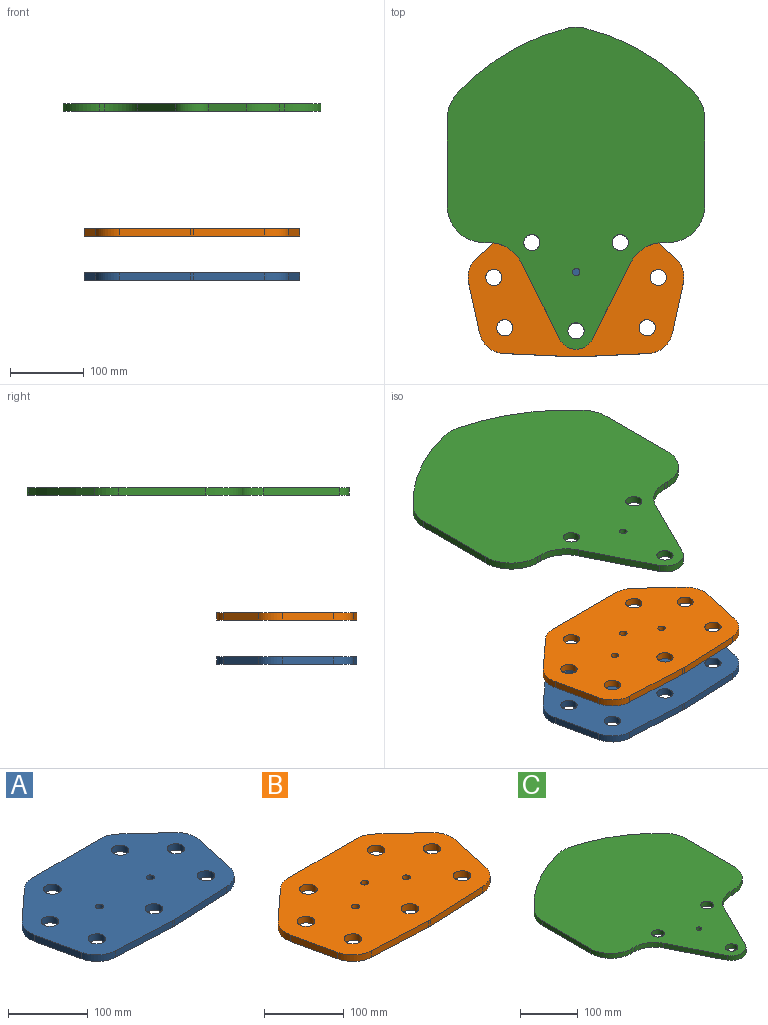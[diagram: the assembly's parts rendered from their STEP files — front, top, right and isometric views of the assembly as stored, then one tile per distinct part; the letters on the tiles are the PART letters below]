
ASSEMBLY  parts=3 mates=2
PART A: 25 faces, bbox 293.4x190x10 mm
  f0: cylinder r=35mm len=10mm, axis (0,0,-1), area 32.2mm2, adj f1,f20,f23,f24
  f1: plane 96.71x10mm, normal (0.05,-1,0), area 968.2mm2, adj f0,f2,f23,f24
  f2: cylinder r=35mm len=32.58mm, axis (0,0,-1), area 458.1mm2, adj f1,f3,f23,f24
  f3: plane 68.37x15mm, normal (0.98,-0.21,0), area 700mm2, adj f2,f4,f23,f24
  f4: cylinder r=35mm len=33.36mm, axis (0,0,-1), area 366.5mm2, adj f3,f5,f23,f24
  f5: plane 51.71x47.18mm, normal (0.67,0.74,0), area 700mm2, adj f4,f6,f23,f24
  f6: cylinder r=35mm len=23.59mm, axis (0,0,-1), area 258.8mm2, adj f5,f7,f23,f24
  f7: plane 120x10mm, normal (0,1,0), area 1200mm2, adj f6,f8,f23,f24
  f8: cylinder r=35mm len=23.59mm, axis (0,0,-1), area 258.8mm2, adj f7,f9,f23,f24
  f9: plane 51.71x47.18mm, normal (-0.67,0.74,0), area 700mm2, adj f8,f10,f23,f24
  f10: cylinder r=35mm len=33.36mm, axis (0,0,-1), area 366.5mm2, adj f9,f11,f23,f24
  f11: plane 68.37x15mm, normal (-0.98,-0.21,0), area 700mm2, adj f10,f12,f23,f24
  f12: cylinder r=35mm len=32.58mm, axis (0,0,-1), area 458.1mm2, adj f11,f20,f23,f24
  f13: cylinder r=5mm len=10mm, axis (0,0,-1), area 314.2mm2, adj f23,f24
  f14: cylinder r=11mm len=22mm, axis (0,0,-1), area 691.2mm2, adj f23,f24
  f15: cylinder r=11mm len=22mm, axis (0,0,-1), area 691.2mm2, adj f23,f24
  f16: cylinder r=11mm len=22mm, axis (0,0,-1), area 691.2mm2, adj f23,f24
  f17: cylinder r=11mm len=22mm, axis (0,0,-1), area 691.2mm2, adj f23,f24
  f18: cylinder r=11mm len=22mm, axis (0,0,-1), area 691.2mm2, adj f23,f24
  f19: cylinder r=11mm len=22mm, axis (0,0,-1), area 691.2mm2, adj f23,f24
  f20: plane 96.71x10mm, normal (-0.05,-1,0), area 968.2mm2, adj f0,f12,f23,f24
  f21: cylinder r=11mm len=22mm, axis (0,0,-1), area 691.2mm2, adj f23,f24
  f22: cylinder r=5mm len=10mm, axis (0,0,-1), area 314.2mm2, adj f23,f24
  f23: plane 293.43x190mm, normal (0,0,1), area 44589.8mm2, adj f0,f1,f2,f3,f4,f5,f6,f7
  f24: plane 293.43x190mm, normal (0,0,-1), area 44589.8mm2, adj f0,f1,f2,f3,f4,f5,f6,f7
PART B: 26 faces, bbox 293.4x190x10 mm
  f0: cylinder r=35mm len=10mm, axis (0,0,-1), area 32.2mm2, adj f1,f21,f24,f25
  f1: plane 96.71x10mm, normal (0.05,-1,0), area 968.2mm2, adj f0,f2,f24,f25
  f2: cylinder r=35mm len=32.58mm, axis (0,0,-1), area 458.1mm2, adj f1,f3,f24,f25
  f3: plane 68.37x15mm, normal (0.98,-0.21,0), area 700mm2, adj f2,f4,f24,f25
  f4: cylinder r=35mm len=33.36mm, axis (0,0,-1), area 366.5mm2, adj f3,f5,f24,f25
  f5: plane 51.71x47.18mm, normal (0.67,0.74,0), area 700mm2, adj f4,f6,f24,f25
  f6: cylinder r=35mm len=23.59mm, axis (0,0,-1), area 258.8mm2, adj f5,f7,f24,f25
  f7: plane 120x10mm, normal (0,1,0), area 1200mm2, adj f6,f8,f24,f25
  f8: cylinder r=35mm len=23.59mm, axis (0,0,-1), area 258.8mm2, adj f7,f9,f24,f25
  f9: plane 51.71x47.18mm, normal (-0.67,0.74,0), area 700mm2, adj f8,f10,f24,f25
  f10: cylinder r=35mm len=33.36mm, axis (0,0,-1), area 366.5mm2, adj f9,f11,f24,f25
  f11: plane 68.37x15mm, normal (-0.98,-0.21,0), area 700mm2, adj f10,f12,f24,f25
  f12: cylinder r=35mm len=32.58mm, axis (0,0,-1), area 458.1mm2, adj f11,f21,f24,f25
  f13: cylinder r=5mm len=10mm, axis (0,0,-1), area 314.2mm2, adj f24,f25
  f14: cylinder r=5mm len=10mm, axis (0,0,-1), area 314.2mm2, adj f24,f25
  f15: cylinder r=11mm len=22mm, axis (0,0,-1), area 691.2mm2, adj f24,f25
  f16: cylinder r=11mm len=22mm, axis (0,0,-1), area 691.2mm2, adj f24,f25
  f17: cylinder r=11mm len=22mm, axis (0,0,-1), area 691.2mm2, adj f24,f25
  f18: cylinder r=11mm len=22mm, axis (0,0,-1), area 691.2mm2, adj f24,f25
  f19: cylinder r=11mm len=22mm, axis (0,0,-1), area 691.2mm2, adj f24,f25
  f20: cylinder r=11mm len=22mm, axis (0,0,-1), area 691.2mm2, adj f24,f25
  f21: plane 96.71x10mm, normal (-0.05,-1,0), area 968.2mm2, adj f0,f12,f24,f25
  f22: cylinder r=11mm len=22mm, axis (0,0,-1), area 691.2mm2, adj f24,f25
  f23: cylinder r=5mm len=10mm, axis (0,0,-1), area 314.2mm2, adj f24,f25
  f24: plane 293.43x190mm, normal (0,0,1), area 44511.2mm2, adj f0,f1,f2,f3,f4,f5,f6,f7
  f25: plane 293.43x190mm, normal (0,0,-1), area 44511.2mm2, adj f0,f1,f2,f3,f4,f5,f6,f7
PART C: 22 faces, bbox 350x437.7x10 mm
  f0: cylinder r=25mm len=44.72mm, axis (0,0,-1), area 553.6mm2, adj f1,f10,f13,f14
  f1: plane 103.54x51.77mm, normal (0.89,-0.45,0), area 1157.6mm2, adj f0,f13,f14,f16
  f2: plane 10x6.15mm, normal (0,-1,0), area 61.5mm2, adj f13,f14,f16,f17
  f3: plane 118.15x10mm, normal (1,0,0), area 1181.5mm2, adj f13,f14,f17,f18
  f4: cylinder r=300mm len=150mm, axis (0,0,-1), area 1772.1mm2, adj f13,f14,f18,f19
  f5: cylinder r=300mm len=150mm, axis (0,0,-1), area 1772.1mm2, adj f13,f14,f19,f20
  f6: plane 118.15x10mm, normal (-1,0,0), area 1181.5mm2, adj f13,f14,f20,f21
  f7: plane 10x6.15mm, normal (0,-1,0), area 61.5mm2, adj f13,f14,f15,f21
  f8: cylinder r=11mm len=22mm, axis (0,0,-1), area 691.2mm2, adj f13,f14
  f9: cylinder r=11mm len=22mm, axis (0,0,-1), area 691.2mm2, adj f13,f14
  f10: plane 103.54x51.77mm, normal (-0.89,-0.45,0), area 1157.6mm2, adj f0,f13,f14,f15
  f11: cylinder r=11mm len=22mm, axis (0,0,-1), area 691.2mm2, adj f13,f14
  f12: cylinder r=5mm len=10mm, axis (0,0,-1), area 314.2mm2, adj f13,f14
  f13: plane 437.69x350mm, normal (0,0,1), area 101918.3mm2, adj f0,f1,f2,f3,f4,f5,f6,f7
  f14: plane 437.69x350mm, normal (0,0,-1), area 101918.3mm2, adj f0,f1,f2,f3,f4,f5,f6,f7
  f15: cylinder r=50mm len=44.72mm, axis (0,0,1), area 553.6mm2, adj f7,f10,f13,f14
  f16: cylinder r=50mm len=44.72mm, axis (0,0,1), area 553.6mm2, adj f1,f2,f13,f14
  f17: cylinder r=50mm len=50mm, axis (0,0,-1), area 785.4mm2, adj f2,f3,f13,f14
  f18: cylinder r=50mm len=33.63mm, axis (0,0,-1), area 368.9mm2, adj f3,f4,f13,f14
  f19: cylinder r=50mm len=24mm, axis (0,0,-1), area 242.4mm2, adj f4,f5,f13,f14
  f20: cylinder r=50mm len=33.63mm, axis (0,0,-1), area 368.9mm2, adj f5,f6,f13,f14
  f21: cylinder r=50mm len=50mm, axis (0,0,1), area 785.4mm2, adj f6,f7,f13,f14
PLACE A t=(-62.72,-3.77,-11.62)mm
PLACE B t=(-62.72,-3.77,48.38)mm fixed
PLACE C t=(-62.72,-3.77,218.07)mm
MATE fastened B.f22 <-> A.f21  axis (0,0,-1) through (-62.72,-3.77,48.38)mm
MATE slider C.f0 <-> B.f22  axis (0,0,1) through (-62.72,-3.77,228.07)mm
